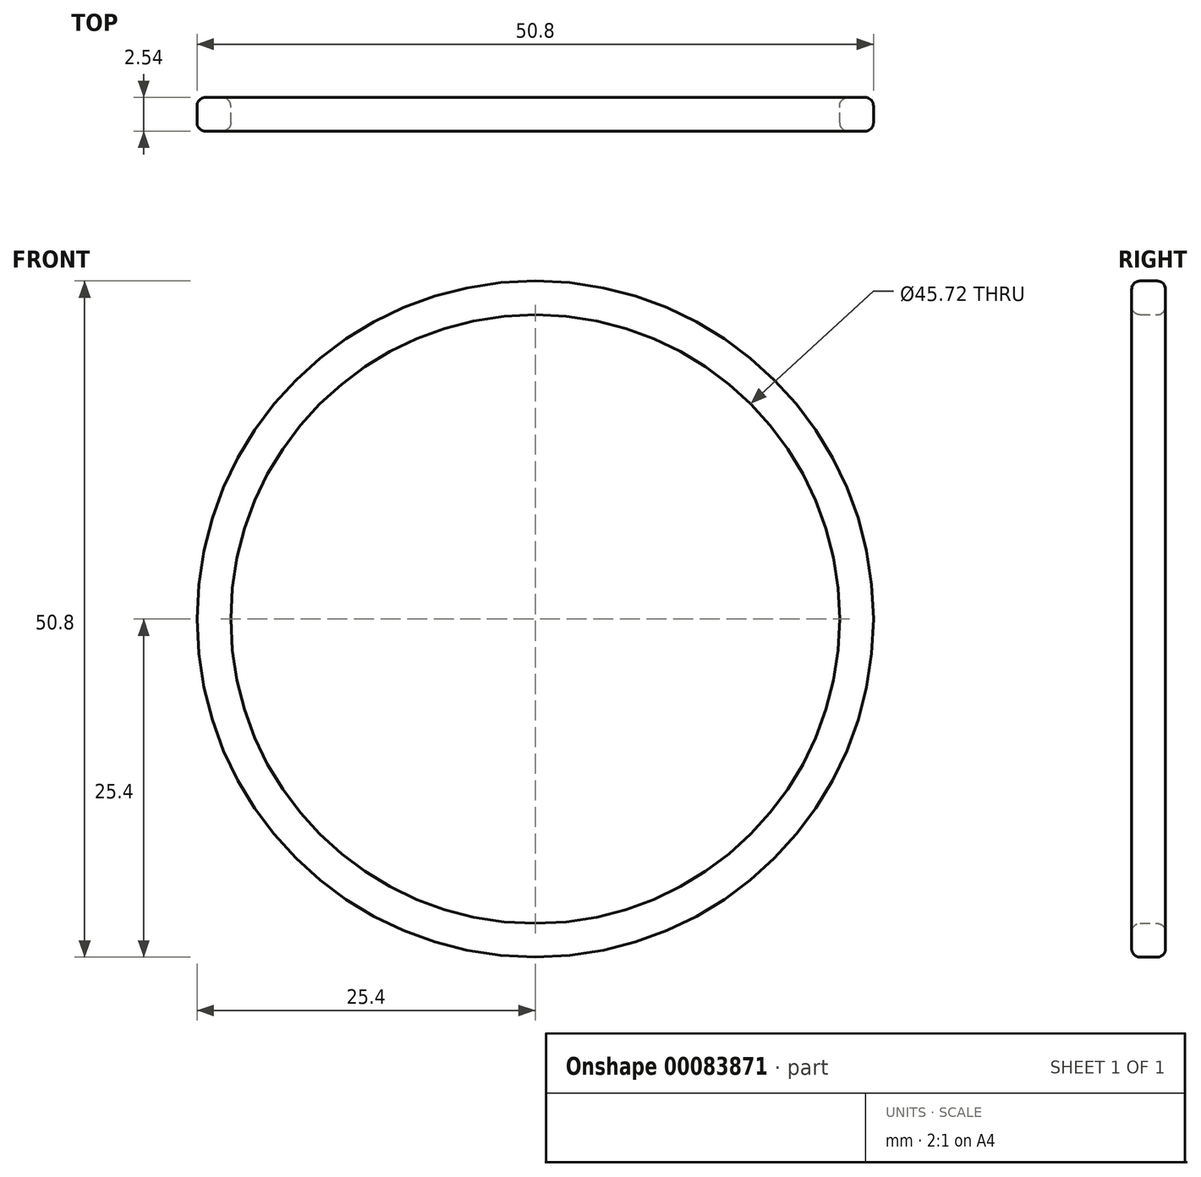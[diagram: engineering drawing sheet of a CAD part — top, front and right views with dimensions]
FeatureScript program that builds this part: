
annotation { "Feature Type Name" : "Feature", "Feature Type Description" : "" }
export const myFeature = defineFeature(function(context is Context, id is Id, definition is map)
    precondition{}
    {
        {
            var Q0;
            Q0=qCreatedBy(makeId("Front.planeOp"),FACE);
            var sketch = newSketch(context, id + "F0", { "sketchPlane" : qUnion([Q0])});
            skCircle(sketch, "E0", {"center": v(0, 0) * mm, "radius": 25.4 * mm});
            skCircle(sketch, "E1", {"center": v(0, 0) * mm, "radius": 22.86 * mm});
            skSolve(sketch);
        }
        {
            var Q0;
            Q0=makeQuery(id+"F0.imprint","IMPRINT",FACE,{"disambiguationData":[TD([[makeQuery(id+"F0.imprint","IMPRINT",EDGE,{"derivedFrom":sQuery(id+"F0.wireOp",EDGE,"E0")}),1.0]])]});
            extrude(context, id + "F1", {"entities" : qUnion([Q0]), "depth" : 2.54 * mm});
        }
        {
            var Q0;
            Q0=makeQuery(id+"F1.opExtrude","CAP_EDGE",EDGE,{"disambiguationData":[OSD([sQuery(id+"F0.wireOp",EDGE,"E1")])],"isStart":false});
            fillet(context, id + "F2", {"entities" : qUnion([Q0]), "radius" : 0.64 * mm, "tangentPropagation" : true, "allowEdgeOverflow" : false});
        }
        {
            var Q0;
            Q0=makeQuery(id+"F1.opExtrude","CAP_EDGE",EDGE,{"disambiguationData":[OSD([sQuery(id+"F0.wireOp",EDGE,"E0")])],"isStart":false});
            fillet(context, id + "F3", {"entities" : qUnion([Q0]), "radius" : 0.64 * mm, "tangentPropagation" : true, "allowEdgeOverflow" : false});
        }
        {
            var Q0;
            Q0=makeQuery(id+"F1.opExtrude","CAP_EDGE",EDGE,{"disambiguationData":[OSD([sQuery(id+"F0.wireOp",EDGE,"E0")])],"isStart":true});
            var Q1;
            Q1=makeQuery(id+"F1.opExtrude","CAP_EDGE",EDGE,{"disambiguationData":[OSD([sQuery(id+"F0.wireOp",EDGE,"E1")])],"isStart":true});
            fillet(context, id + "F4", {"entities" : qUnion([Q0, Q1]), "radius" : 0.64 * mm, "tangentPropagation" : true, "allowEdgeOverflow" : false});
        }
    });
